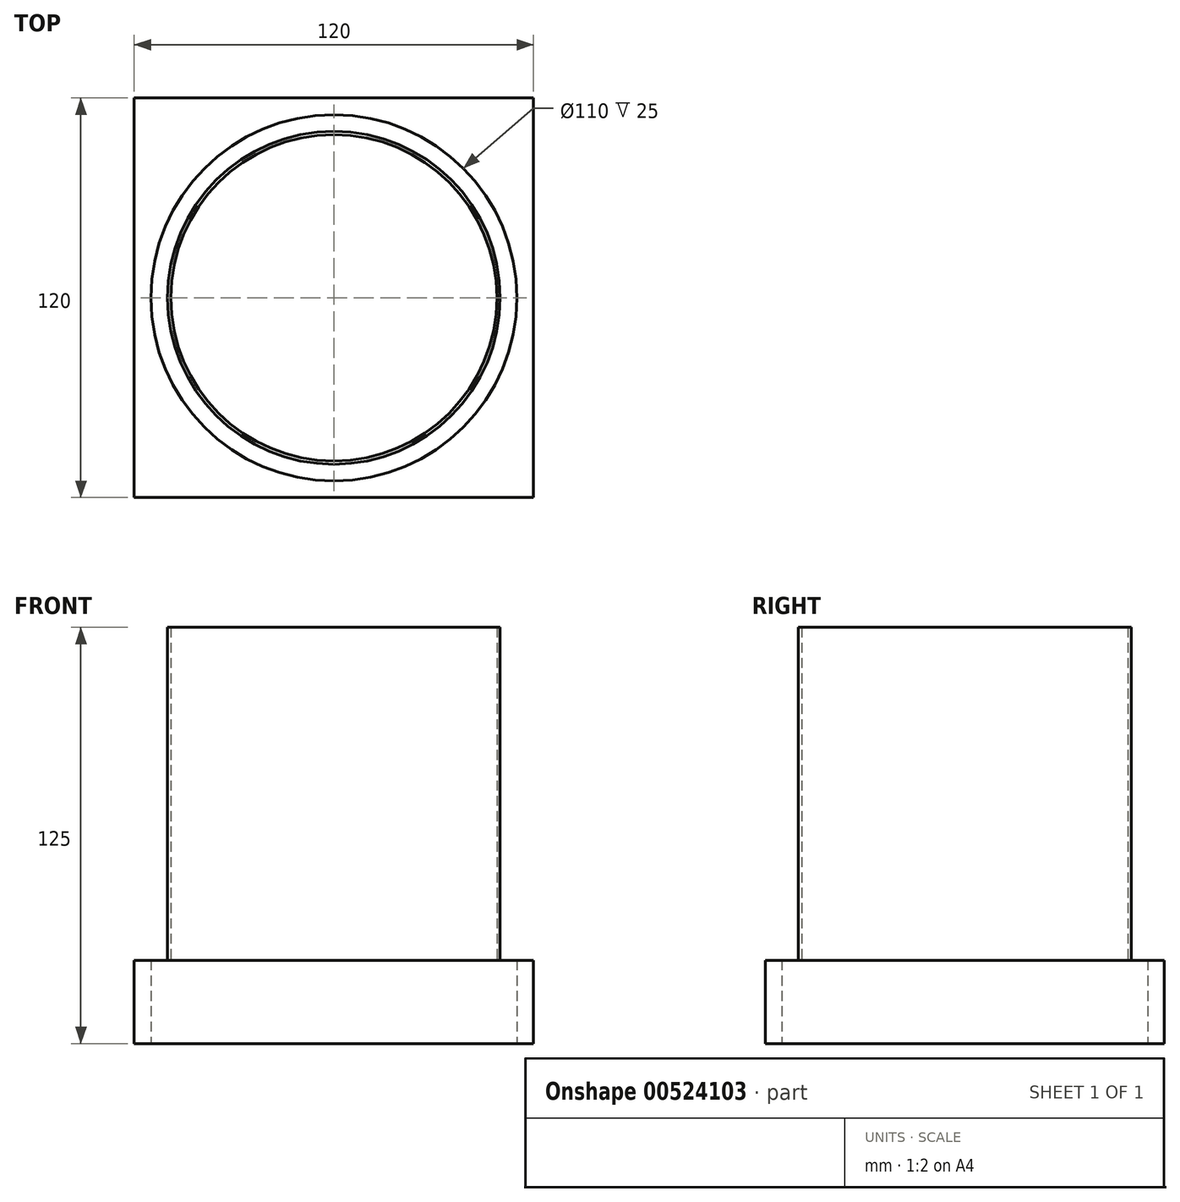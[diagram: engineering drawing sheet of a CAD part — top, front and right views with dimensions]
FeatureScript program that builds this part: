
annotation { "Feature Type Name" : "Feature", "Feature Type Description" : "" }
export const myFeature = defineFeature(function(context is Context, id is Id, definition is map)
    precondition{}
    {
        {
            var Q0;
            Q0=qCreatedBy(makeId("Top.planeOp"),FACE);
            var sketch = newSketch(context, id + "F0", { "sketchPlane" : qUnion([Q0])});
            skLineSegment(sketch, "E0.bottom", {"start": v(-60, 60) * mm, "end": v(60, 60) * mm});
            skLineSegment(sketch, "E0.top", {"start": v(-60, -60) * mm, "end": v(60, -60) * mm});
            skLineSegment(sketch, "E0.left", {"start": v(-60, 60) * mm, "end": v(-60, -60) * mm});
            skLineSegment(sketch, "E0.right", {"start": v(60, 60) * mm, "end": v(60, -60) * mm});
            skPoint(sketch, "E0.middle", {"position": v(0, 0) * mm});
            skCircle(sketch, "E1", {"center": v(0, 0) * mm, "radius": 55 * mm});
            skSolve(sketch);
        }
        {
            var Q0;
            Q0 = qSketchRegion(id + "F0", true);
            extrude(context, id + "F1", {"entities" : qUnion([Q0]), "depth" : 25 * mm, "offsetDistance" : 25 * mm});
        }
        {
            var Q0;
            Q0=makeQuery(id+"F1.opExtrude","CAP_FACE",FACE,{"disambiguationData":[OSD([sQuery(id+"F0.wireOp",EDGE,"E0.bottom"),sQuery(id+"F0.wireOp",EDGE,"E0.top"),sQuery(id+"F0.wireOp",EDGE,"E0.left"),sQuery(id+"F0.wireOp",EDGE,"E0.right"),sQuery(id+"F0.wireOp",EDGE,"E1")])],"isStart":false});
            var sketch = newSketch(context, id + "F2", { "sketchPlane" : qUnion([Q0])});
            skCircle(sketch, "E2", {"center": v(0, 0) * mm, "radius": 50 * mm});
            skCircle(sketch, "E3", {"center": v(0, 0) * mm, "radius": 49 * mm});
            skSolve(sketch);
        }
        {
            var Q0;
            Q0 = qSketchRegion(id + "F2", true);
            extrude(context, id + "F3", {"entities" : qUnion([Q0]), "depth" : 100 * mm, "offsetDistance" : 25 * mm});
        }
    });
